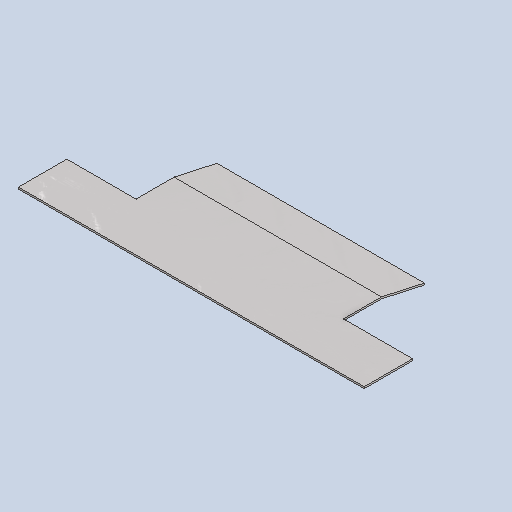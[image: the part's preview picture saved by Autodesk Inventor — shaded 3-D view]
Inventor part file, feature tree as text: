
AUTODESK INVENTOR PART (.ipt)
format: ipt  version: 2023 (Build 270158000, 158)  size: 244,224 bytes
history: native  units: mm
features: extrude x3, sketch x3, other x1, projected_geometry x1
ambient origin geometry x8: Origin, YZ Plane, XZ Plane, XY Plane, X Axis, Y Axis, Z Axis, Center Point
bodies: Body1 (feature_tree)
feature tree (8):
  other  "Bryła1"
  extrude  "Wyciągnięcie proste1"  Depth=100.0mm
  extrude  "Wyciągnięcie proste2"  Depth=14.0mm
  extrude  "Wyciągnięcie proste3"  Depth=0.5mm TaperAngle=0.0deg
  sketch  "Szkic1"
  sketch  "Szkic2"
  sketch  "Szkic3"
  projected_geometry  "Pętla rzutowana1"
